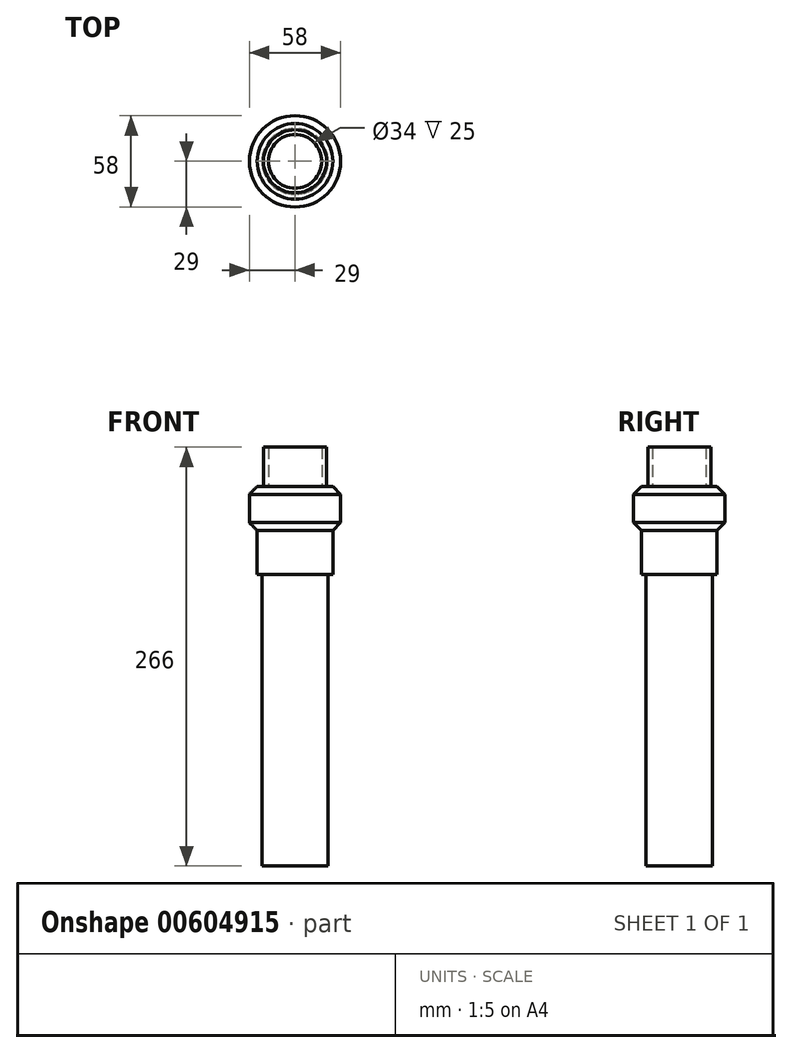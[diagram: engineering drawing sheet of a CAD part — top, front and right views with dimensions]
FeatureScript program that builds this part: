
annotation { "Feature Type Name" : "Feature", "Feature Type Description" : "" }
export const myFeature = defineFeature(function(context is Context, id is Id, definition is map)
    precondition{}
    {
        {
            var Q0;
            Q0=qCreatedBy(makeId("Top.planeOp"),FACE);
            var sketch = newSketch(context, id + "F0", { "sketchPlane" : qUnion([Q0])});
            skCircle(sketch, "E0", {"center": v(0, 0) * mm, "radius": 21 * mm});
            skSolve(sketch);
        }
        {
            var Q0;
            Q0=qSketchRegion(id+"F0",true);
            extrude(context, id + "F1", {"entities" : qUnion([Q0]), "depth" : 200 * mm, "offsetDistance" : 25 * mm});
        }
        {
            var Q0;
            Q0=qCreatedBy(makeId("Front.planeOp"),FACE);
            var sketch = newSketch(context, id + "F2", { "sketchPlane" : qUnion([Q0])});
            skLineSegment(sketch, "E1", {"start": v(0, 0) * mm, "end": v(0, 149.12) * mm, "construction": true});
            skLineSegment(sketch, "E2", {"start": v(0, 185) * mm, "end": v(-24, 185) * mm});
            skLineSegment(sketch, "E3", {"start": v(-24, 185) * mm, "end": v(-24, 213) * mm});
            skLineSegment(sketch, "E4", {"start": v(-24, 213) * mm, "end": v(-29, 218) * mm});
            skLineSegment(sketch, "E5", {"start": v(-29, 218) * mm, "end": v(-29, 236) * mm});
            skLineSegment(sketch, "E6", {"start": v(-29, 236) * mm, "end": v(-24, 241) * mm});
            skLineSegment(sketch, "E7", {"start": v(-24, 241) * mm, "end": v(0, 241) * mm});
            skLineSegment(sketch, "E8", {"start": v(0, 241) * mm, "end": v(0, 185) * mm});
            skSolve(sketch);
        }
        {
            var Q0;
            Q0 = qSketchRegion(id + "F2", true);
            var Q1;
            Q1=sQuery(id+"F2.wireOp",EDGE,"E1");
            revolve(context, id + "F3", {"operationType" : NewBodyOperationType.ADD, "entities" : qUnion([Q0]), "axis" : qUnion([Q1]), "revolveType" : RevolveType.FULL});
        }
        {
            var Q0;
            Q0=makeQuery(id+"F3.opRevolve","SWEPT_FACE",FACE,{"disambiguationData":[OSD([sQuery(id+"F2.wireOp",EDGE,"E7")])]});
            var sketch = newSketch(context, id + "F4", { "sketchPlane" : qUnion([Q0])});
            skCircle(sketch, "E9", {"center": v(0, 0) * mm, "radius": 20 * mm});
            skCircle(sketch, "E10", {"center": v(0, 0) * mm, "radius": 17 * mm});
            skSolve(sketch);
        }
        {
            var Q0;
            Q0 = qSketchRegion(id + "F4", true);
            extrude(context, id + "F5", {"entities" : qUnion([Q0]), "operationType" : NewBodyOperationType.ADD, "depth" : 25 * mm, "offsetDistance" : 25 * mm});
        }
    });
